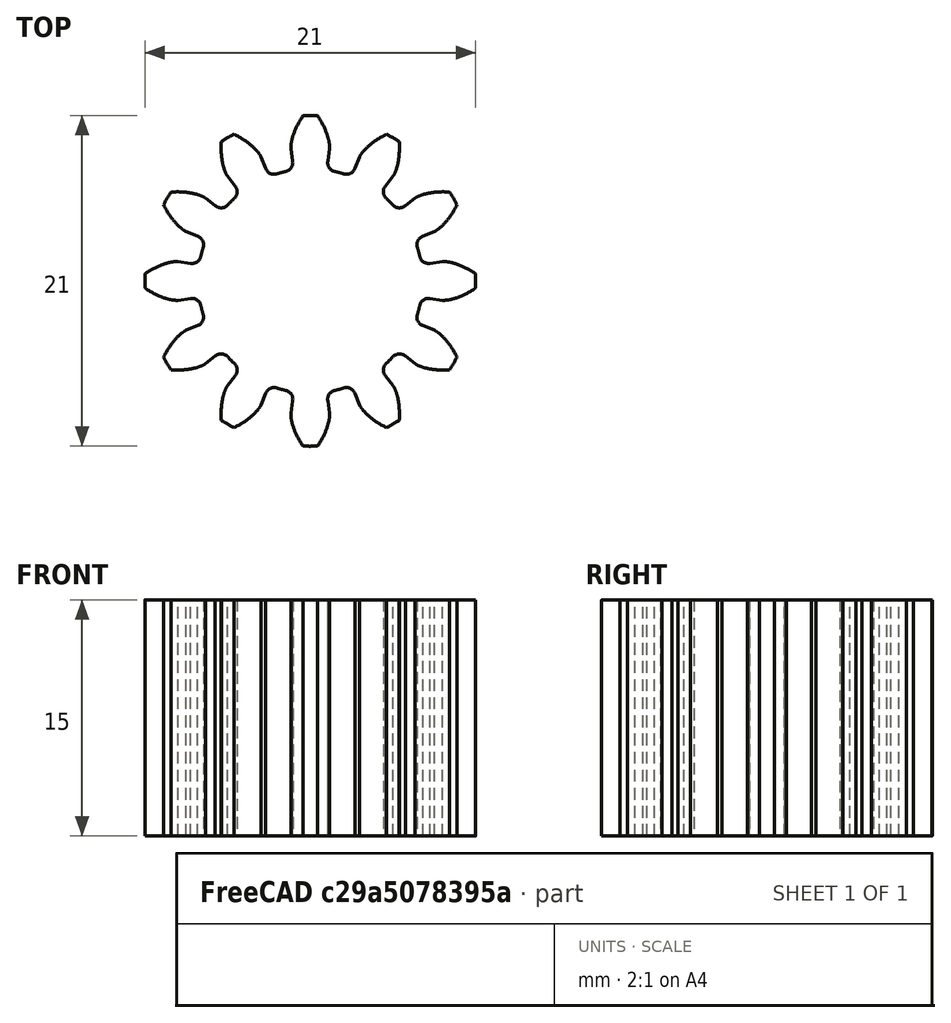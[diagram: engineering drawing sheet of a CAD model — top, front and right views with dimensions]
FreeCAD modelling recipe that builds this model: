
FCSTD DOCUMENT  (FreeCAD 1.0R39319 (Git))
Label: inv gear t12 m1_5 w15
License: All rights reserved
LicenseURL: https://en.wikipedia.org/wiki/All_rights_reserved
objects: Part::Part2DObjectPython×1, PartDesign::Pad×1, PartDesign::Body×1
note: 5 computed .brp shape members not serialized (recipe doc carries the construction recipe); baked Part::Feature solids carry a one-line shape summary decoded from their .brp

FEATURE [Part::Part2DObjectPython] InvoluteGear  # Draft 2D object (typed FeaturePython)
  AddendumCoefficient = 1
  DedendumCoefficient = 1.25
  ExternalGear = true
  HighPrecision = true
  Modules = 1.5
  NumberOfTeeth = 12
  PressureAngle = 20
  ProfileShiftCoefficient = 0
  RootFilletCoefficient = 0.38
FEATURE [PartDesign::Pad] Pad
  Direction = (0,0,1)
  Length = 15
  Length2 = 10
  Profile = -> InvoluteGear
  ReferenceAxis = -> InvoluteGear [N_Axis]
  Refine = true
  Suppressed = false
  Type = 0
FEATURE [PartDesign::Body] Body
  AllowCompound = false
  Group = -> [InvoluteGear,Pad]
  Origin = -> Origin
  Tip = -> Pad
